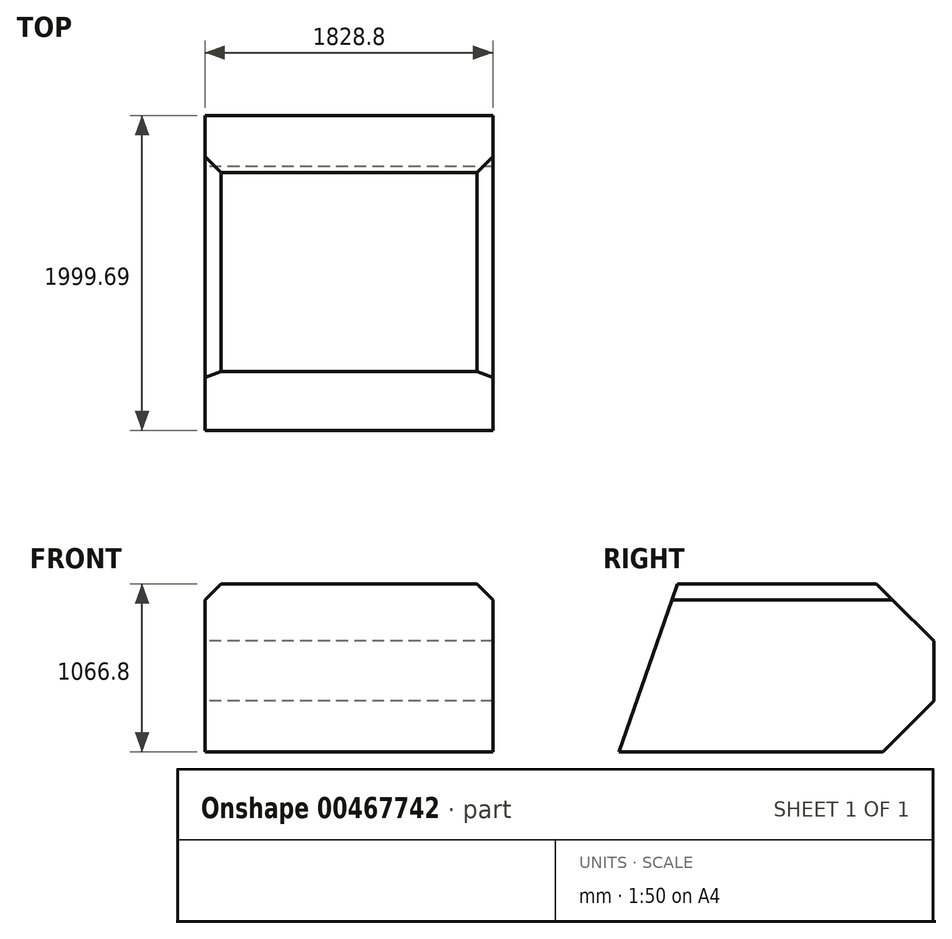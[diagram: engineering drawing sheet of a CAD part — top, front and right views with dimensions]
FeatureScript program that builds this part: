
annotation { "Feature Type Name" : "Feature", "Feature Type Description" : "" }
export const myFeature = defineFeature(function(context is Context, id is Id, definition is map)
    precondition{}
    {
        {
            var Q0;
            Q0=qCreatedBy(makeId("Right.planeOp"),FACE);
            var sketch = newSketch(context, id + "F0", { "sketchPlane" : qUnion([Q0])});
            skLineSegment(sketch, "E0.top", {"start": v(-1700.79, -307.83) * mm, "end": v(-24.39, -307.83) * mm});
            skLineSegment(sketch, "E1", {"start": v(-63.61, 758.97) * mm, "end": v(298.9, 396.46) * mm});
            skLineSegment(sketch, "E2", {"start": v(298.9, 396.46) * mm, "end": v(298.9, 15.46) * mm});
            skLineSegment(sketch, "E3", {"start": v(298.9, 15.46) * mm, "end": v(-24.39, -307.83) * mm});
            skLineSegment(sketch, "E4", {"start": v(-1700.79, -307.83) * mm, "end": v(-1327.78, 758.97) * mm});
            skLineSegment(sketch, "E5", {"start": v(-1327.78, 758.97) * mm, "end": v(-63.61, 758.97) * mm});
            skSolve(sketch);
        }
        {
            var Q0;
            Q0 = qSketchRegion(id + "F0", true);
            extrude(context, id + "F1", {"entities" : qUnion([Q0]), "depth" : 1828.8 * mm});
        }
        {
            var Q0;
            Q0=makeQuery(id+"F1.opExtrude","SWEPT_FACE",FACE,{"disambiguationData":[OSD([sQuery(id+"F0.wireOp",EDGE,"E1")])]});
            var sketch = newSketch(context, id + "F2", { "sketchPlane" : qUnion([Q0])});
            skSolve(sketch);
        }
        {
            var Q0;
            Q0=makeQuery(id+"F1.opExtrude","CAP_EDGE",EDGE,{"disambiguationData":[OSD([sQuery(id+"F0.wireOp",EDGE,"E5")])],"isStart":false});
            chamfer(context, id + "F3", {"entities" : qUnion([Q0]), "width" : 101.6 * mm, "tangentPropagation" : true});
        }
        {
            var Q0;
            Q0=makeQuery(id+"F1.opExtrude","CAP_EDGE",EDGE,{"disambiguationData":[OSD([sQuery(id+"F0.wireOp",EDGE,"E5")])],"isStart":true});
            chamfer(context, id + "F4", {"entities" : qUnion([Q0]), "width" : 101.6 * mm, "tangentPropagation" : true});
        }
    });
